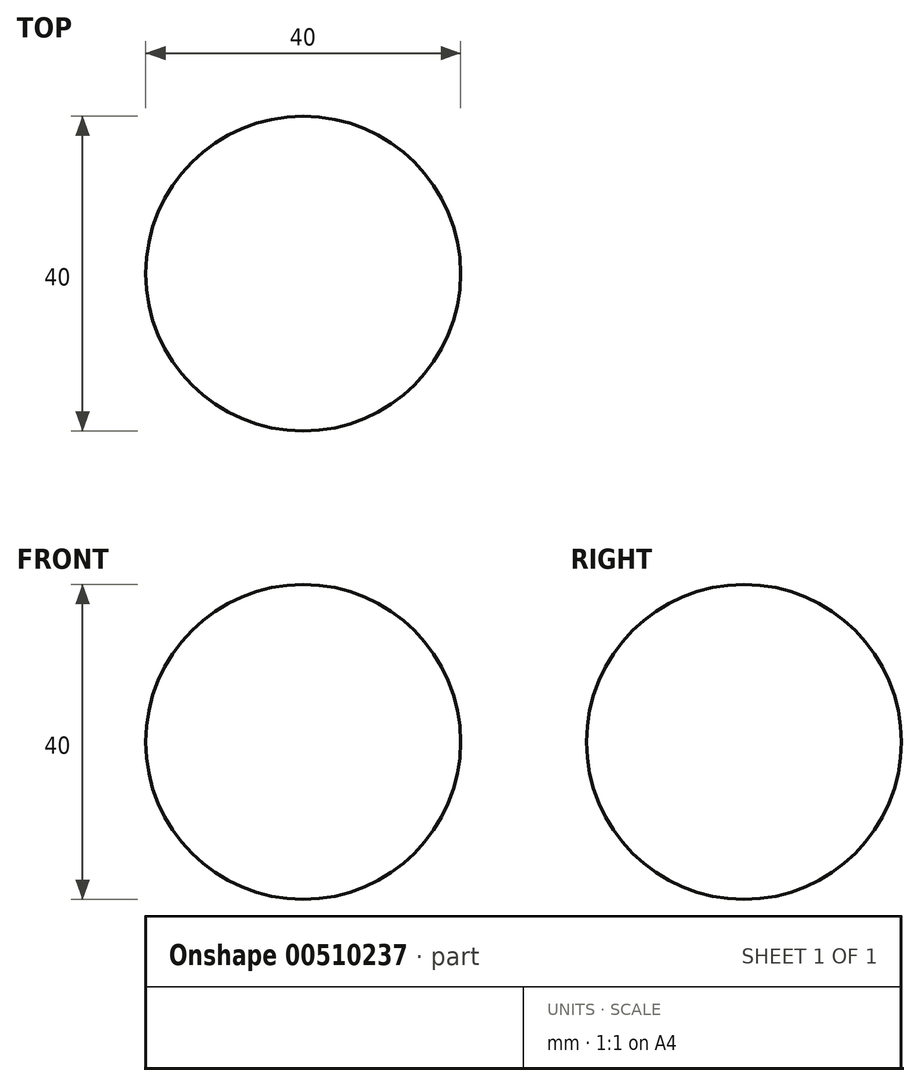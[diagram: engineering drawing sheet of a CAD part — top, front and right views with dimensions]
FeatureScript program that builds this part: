
annotation { "Feature Type Name" : "Feature", "Feature Type Description" : "" }
export const myFeature = defineFeature(function(context is Context, id is Id, definition is map)
    precondition{}
    {
        {
            var Q0;
            Q0=qCreatedBy(makeId("Top.planeOp"),FACE);
            var sketch = newSketch(context, id + "F0", { "sketchPlane" : qUnion([Q0])});
            skLineSegment(sketch, "E0.bottom", {"start": v(-48.96, 49.84) * mm, "end": v(-8.96, 49.84) * mm});
            skLineSegment(sketch, "E0.top", {"start": v(-48.96, 9.84) * mm, "end": v(-8.96, 9.84) * mm});
            skLineSegment(sketch, "E0.left", {"start": v(-48.96, 49.84) * mm, "end": v(-48.96, 9.84) * mm});
            skLineSegment(sketch, "E0.right", {"start": v(-8.96, 49.84) * mm, "end": v(-8.96, 9.84) * mm});
            skSolve(sketch);
        }
        {
            var Q0;
            Q0=makeQuery(id+"F0.imprint","IMPRINT",FACE,{"disambiguationData":[TD([[makeQuery(id+"F0.imprint","IMPRINT",EDGE,{"derivedFrom":sQuery(id+"F0.wireOp",EDGE,"E0.bottom")}),-1.0]])]});
            extrude(context, id + "F1", {"entities" : qUnion([Q0]), "depth" : 40 * mm, "offsetDistance" : 25 * mm});
        }
        {
            var Q0;
            Q0=makeQuery(id+"F1.opExtrude","SWEPT_EDGE",EDGE,{"disambiguationData":[OSD([sQuery(id+"F0.wireOp",EDGE,"E0.bottom"),sQuery(id+"F0.wireOp",EDGE,"E0.right")])]});
            var Q1;
            Q1=makeQuery(id+"F1.opExtrude","SWEPT_EDGE",EDGE,{"disambiguationData":[OSD([sQuery(id+"F0.wireOp",EDGE,"E0.top"),sQuery(id+"F0.wireOp",EDGE,"E0.left")])]});
            var Q2;
            Q2=makeQuery(id+"F1.opExtrude","SWEPT_FACE",FACE,{"disambiguationData":[OSD([sQuery(id+"F0.wireOp",EDGE,"E0.bottom")])]});
            var Q3;
            Q3=makeQuery(id+"F1.opExtrude","SWEPT_EDGE",EDGE,{"disambiguationData":[OSD([sQuery(id+"F0.wireOp",EDGE,"E0.bottom"),sQuery(id+"F0.wireOp",EDGE,"E0.left")])]});
            var Q4;
            Q4=makeQuery(id+"F1.opExtrude","CAP_EDGE",EDGE,{"disambiguationData":[OSD([sQuery(id+"F0.wireOp",EDGE,"E0.bottom")])],"isStart":false});
            var Q5;
            Q5=makeQuery(id+"F1.opExtrude","CAP_FACE",FACE,{"disambiguationData":[OSD([sQuery(id+"F0.wireOp",EDGE,"E0.bottom"),sQuery(id+"F0.wireOp",EDGE,"E0.top"),sQuery(id+"F0.wireOp",EDGE,"E0.left"),sQuery(id+"F0.wireOp",EDGE,"E0.right")])],"isStart":false});
            var Q6;
            Q6=makeQuery(id+"F1.opExtrude","SWEPT_FACE",FACE,{"disambiguationData":[OSD([sQuery(id+"F0.wireOp",EDGE,"E0.left")])]});
            var Q7;
            Q7=makeQuery(id+"F1.opExtrude","SWEPT_FACE",FACE,{"disambiguationData":[OSD([sQuery(id+"F0.wireOp",EDGE,"E0.right")])]});
            var Q8;
            Q8=makeQuery(id+"F1.opExtrude","CAP_EDGE",EDGE,{"disambiguationData":[OSD([sQuery(id+"F0.wireOp",EDGE,"E0.left")])],"isStart":false});
            var Q9;
            Q9=makeQuery(id+"F1.opExtrude","CAP_EDGE",EDGE,{"disambiguationData":[OSD([sQuery(id+"F0.wireOp",EDGE,"E0.right")])],"isStart":false});
            var Q10;
            Q10=makeQuery(id+"F1.opExtrude","SWEPT_FACE",FACE,{"disambiguationData":[OSD([sQuery(id+"F0.wireOp",EDGE,"E0.top")])]});
            var Q11;
            Q11=makeQuery(id+"F1.opExtrude","CAP_EDGE",EDGE,{"disambiguationData":[OSD([sQuery(id+"F0.wireOp",EDGE,"E0.top")])],"isStart":false});
            fillet(context, id + "F2", {"entities" : qUnion([Q0, Q1, Q2, Q3, Q4, Q5, Q6, Q7, Q8, Q9, Q10, Q11]), "radius" : 20 * mm, "tangentPropagation" : true, "allowEdgeOverflow" : false});
        }
    });
